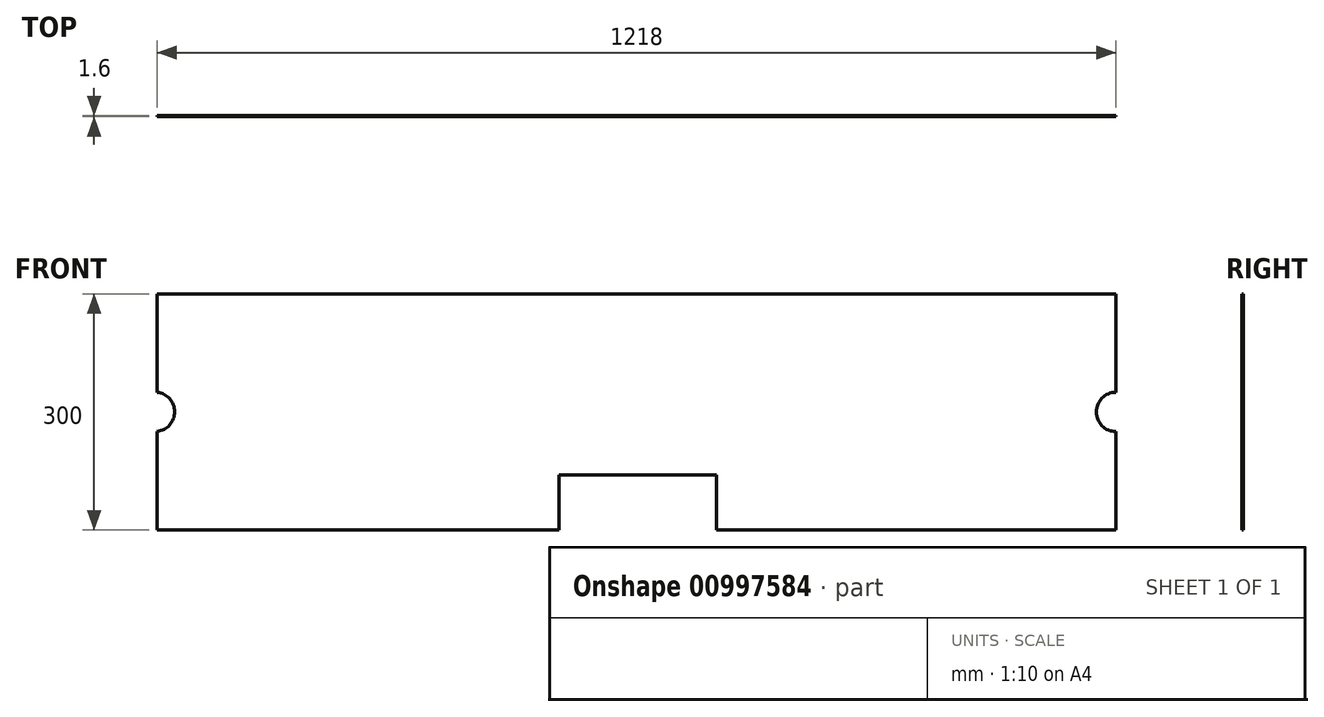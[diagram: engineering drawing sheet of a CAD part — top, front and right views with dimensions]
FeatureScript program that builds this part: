
annotation { "Feature Type Name" : "Feature", "Feature Type Description" : "" }
export const myFeature = defineFeature(function(context is Context, id is Id, definition is map)
    precondition{}
    {
        {
            var Q0;
            Q0=qCreatedBy(makeId("Front.planeOp"),FACE);
            var sketch = newSketch(context, id + "F0", { "sketchPlane" : qUnion([Q0])});
            skLineSegment(sketch, "E0.top", {"start": v(609, 150) * mm, "end": v(-609, 150) * mm});
            skLineSegment(sketch, "E0.left", {"start": v(609, -150) * mm, "end": v(609, 150) * mm});
            skLineSegment(sketch, "E0.right", {"start": v(-609, -150) * mm, "end": v(-609, 150) * mm});
            skPoint(sketch, "E0.middle", {"position": v(0, 0) * mm});
            skLineSegment(sketch, "E1", {"start": v(-609, -150) * mm, "end": v(-98.22, -150) * mm});
            skLineSegment(sketch, "E2", {"start": v(101.78, -150) * mm, "end": v(609, -150) * mm});
            skLineSegment(sketch, "E3", {"start": v(-98.22, -150) * mm, "end": v(-98.22, -80) * mm});
            skLineSegment(sketch, "E4", {"start": v(-98.22, -80) * mm, "end": v(101.78, -80) * mm});
            skLineSegment(sketch, "E5", {"start": v(101.78, -80) * mm, "end": v(101.78, -150) * mm});
            skSolve(sketch);
        }
        {
            var Q0;
            Q0 = qSketchRegion(id + "F0", true);
            extrude(context, id + "F1", {"entities" : qUnion([Q0]), "depth" : 1.6 * mm, "offsetDistance" : 25 * mm, "symmetric" : true});
        }
        {
            var Q0;
            Q0=makeQuery(id+"F1.opExtrude","CAP_FACE",FACE,{"disambiguationData":[OSD([sQuery(id+"F0.wireOp",EDGE,"E0.top"),sQuery(id+"F0.wireOp",EDGE,"E0.left"),sQuery(id+"F0.wireOp",EDGE,"E0.right"),sQuery(id+"F0.wireOp",EDGE,"E1"),sQuery(id+"F0.wireOp",EDGE,"E2"),sQuery(id+"F0.wireOp",EDGE,"E3"),sQuery(id+"F0.wireOp",EDGE,"E4"),sQuery(id+"F0.wireOp",EDGE,"E5")])],"isStart":false});
            var sketch = newSketch(context, id + "F2", { "sketchPlane" : qUnion([Q0])});
            skLineSegment(sketch, "E6", {"start": v(0, 0) * mm, "end": v(-609, 0) * mm});
            skLineSegment(sketch, "E7", {"start": v(0, 0) * mm, "end": v(609, 0) * mm});
            skLineSegment(sketch, "E8", {"start": v(-609, 0) * mm, "end": v(-435, 0) * mm});
            skLineSegment(sketch, "E9", {"start": v(-435, 0) * mm, "end": v(-261, 0) * mm});
            skLineSegment(sketch, "E10", {"start": v(-261, 0) * mm, "end": v(-87, 0) * mm});
            skLineSegment(sketch, "E11", {"start": v(-87, 0) * mm, "end": v(87, 0) * mm});
            skLineSegment(sketch, "E12", {"start": v(87, 0) * mm, "end": v(261, 0) * mm});
            skLineSegment(sketch, "E13", {"start": v(261, 0) * mm, "end": v(435, 0) * mm});
            skLineSegment(sketch, "E14", {"start": v(435, 0) * mm, "end": v(609, 0) * mm});
            skCircle(sketch, "E15", {"center": v(-435, 0) * mm, "radius": 25 * mm});
            skCircle(sketch, "E16", {"center": v(-261, 0) * mm, "radius": 25 * mm});
            skCircle(sketch, "E17", {"center": v(-87, 0) * mm, "radius": 25 * mm});
            skCircle(sketch, "E18", {"center": v(87, 0) * mm, "radius": 25 * mm});
            skCircle(sketch, "E19", {"center": v(261, 0) * mm, "radius": 25 * mm});
            skCircle(sketch, "E20", {"center": v(435, 0) * mm, "radius": 25 * mm});
            skLineSegment(sketch, "E21", {"start": v(-609, 0) * mm, "end": v(-609, 25) * mm});
            skLineSegment(sketch, "E22", {"start": v(609, 0) * mm, "end": v(609, 0) * mm});
            skLineSegment(sketch, "E23", {"start": v(609, 0) * mm, "end": v(609, 25) * mm});
            skLineSegment(sketch, "E24", {"start": v(609, 0) * mm, "end": v(609, -25) * mm});
            skLineSegment(sketch, "E25", {"start": v(-609, 0) * mm, "end": v(-609, -24.7) * mm});
            skArc(sketch, "E26", {"start": v(-609, -24.7) * mm, "mid": v(-586.71, 0.15) * mm, "end": v(-609, 25) * mm});
            skArc(sketch, "E27", {"start": v(609, 25) * mm, "mid": v(584, 0) * mm, "end": v(609, -25) * mm});
            skCircle(sketch, "E28", {"center": v(-522, 0) * mm, "radius": 10 * mm});
            skCircle(sketch, "E29", {"center": v(-348, 0) * mm, "radius": 10 * mm});
            skCircle(sketch, "E30", {"center": v(-174, 0) * mm, "radius": 10 * mm});
            skCircle(sketch, "E31", {"center": v(0, 0) * mm, "radius": 10 * mm});
            skCircle(sketch, "E32", {"center": v(174, 0) * mm, "radius": 10 * mm});
            skCircle(sketch, "E33", {"center": v(348, 0) * mm, "radius": 10 * mm});
            skCircle(sketch, "E34", {"center": v(522, 0) * mm, "radius": 10 * mm});
            skSolve(sketch);
        }
        {
            var Q0;
            {var subQ0=sQuery(id+"F2.wireOp",EDGE,"E21");Q0=makeQuery(id+"F2.imprint","IMPRINT",FACE,{"disambiguationData":[TD([[makeQuery(id+"F2.imprint","IMPRINT",EDGE,{"derivedFrom":subQ0}),-1.0]])]});}
            var Q1;
            {var subQ0=sQuery(id+"F2.wireOp",EDGE,"a51MetO8-heOr-o6G2-Rjjk-PA0d4MG9AU0j");Q1=makeQuery(id+"F2.imprint","IMPRINT",FACE,{"disambiguationData":[TD([[makeQuery(id+"F2.imprint","IMPRINT",EDGE,{"derivedFrom":subQ0}),-1.0]])]});}
            var Q2;
            {var subQ0=sQuery(id+"F2.wireOp",EDGE,"E9");var subQ1=sQuery(id+"F2.wireOp",EDGE,"E8");var subQ2=makeQuery(id+"F2.imprint","INTERSECT",VERTEX,{"derivedFrom":[subQ1,subQ0]});Q2=makeQuery(id+"F2.imprint","IMPRINT",FACE,{"disambiguationData":[TD([[makeQuery(id+"F2.imprint","IMPRINT",EDGE,{"disambiguationData":[TD([[subQ2,1.0]])],"derivedFrom":subQ1}),1.0]])]});}
            var Q3;
            {var subQ0=sQuery(id+"F2.wireOp",EDGE,"E9");var subQ1=sQuery(id+"F2.wireOp",EDGE,"E8");var subQ2=makeQuery(id+"F2.imprint","INTERSECT",VERTEX,{"derivedFrom":[subQ1,subQ0]});Q3=makeQuery(id+"F2.imprint","IMPRINT",FACE,{"disambiguationData":[TD([[makeQuery(id+"F2.imprint","IMPRINT",EDGE,{"disambiguationData":[TD([[subQ2,1.0]])],"derivedFrom":subQ1}),-1.0]])]});}
            var Q4;
            {var subQ0=sQuery(id+"F2.wireOp",EDGE,"E10");var subQ1=sQuery(id+"F2.wireOp",EDGE,"E9");var subQ2=makeQuery(id+"F2.imprint","INTERSECT",VERTEX,{"derivedFrom":[subQ1,subQ0]});Q4=makeQuery(id+"F2.imprint","IMPRINT",FACE,{"disambiguationData":[TD([[makeQuery(id+"F2.imprint","IMPRINT",EDGE,{"disambiguationData":[TD([[subQ2,1.0]])],"derivedFrom":subQ1}),1.0]])]});}
            var Q5;
            {var subQ0=sQuery(id+"F2.wireOp",EDGE,"E10");var subQ1=sQuery(id+"F2.wireOp",EDGE,"E9");var subQ2=makeQuery(id+"F2.imprint","INTERSECT",VERTEX,{"derivedFrom":[subQ1,subQ0]});Q5=makeQuery(id+"F2.imprint","IMPRINT",FACE,{"disambiguationData":[TD([[makeQuery(id+"F2.imprint","IMPRINT",EDGE,{"disambiguationData":[TD([[subQ2,1.0]])],"derivedFrom":subQ1}),-1.0]])]});}
            var Q6;
            {var subQ0=sQuery(id+"F2.wireOp",EDGE,"E11");var subQ1=sQuery(id+"F2.wireOp",EDGE,"E10");var subQ2=makeQuery(id+"F2.imprint","INTERSECT",VERTEX,{"derivedFrom":[subQ1,subQ0]});Q6=makeQuery(id+"F2.imprint","IMPRINT",FACE,{"disambiguationData":[TD([[makeQuery(id+"F2.imprint","IMPRINT",EDGE,{"disambiguationData":[TD([[subQ2,1.0]])],"derivedFrom":subQ1}),1.0]])]});}
            var Q7;
            {var subQ0=sQuery(id+"F2.wireOp",EDGE,"E11");var subQ1=sQuery(id+"F2.wireOp",EDGE,"E10");var subQ2=makeQuery(id+"F2.imprint","INTERSECT",VERTEX,{"derivedFrom":[subQ1,subQ0]});Q7=makeQuery(id+"F2.imprint","IMPRINT",FACE,{"disambiguationData":[TD([[makeQuery(id+"F2.imprint","IMPRINT",EDGE,{"disambiguationData":[TD([[subQ2,1.0]])],"derivedFrom":subQ1}),-1.0]])]});}
            var Q8;
            {var subQ0=sQuery(id+"F2.wireOp",EDGE,"E12");var subQ1=sQuery(id+"F2.wireOp",EDGE,"E11");var subQ2=makeQuery(id+"F2.imprint","INTERSECT",VERTEX,{"derivedFrom":[subQ1,subQ0]});Q8=makeQuery(id+"F2.imprint","IMPRINT",FACE,{"disambiguationData":[TD([[makeQuery(id+"F2.imprint","IMPRINT",EDGE,{"disambiguationData":[TD([[subQ2,1.0]])],"derivedFrom":subQ1}),1.0]])]});}
            var Q9;
            {var subQ0=sQuery(id+"F2.wireOp",EDGE,"E12");var subQ1=sQuery(id+"F2.wireOp",EDGE,"E11");var subQ2=makeQuery(id+"F2.imprint","INTERSECT",VERTEX,{"derivedFrom":[subQ1,subQ0]});Q9=makeQuery(id+"F2.imprint","IMPRINT",FACE,{"disambiguationData":[TD([[makeQuery(id+"F2.imprint","IMPRINT",EDGE,{"disambiguationData":[TD([[subQ2,1.0]])],"derivedFrom":subQ1}),-1.0]])]});}
            var Q10;
            {var subQ0=sQuery(id+"F2.wireOp",EDGE,"E13");var subQ1=sQuery(id+"F2.wireOp",EDGE,"E12");var subQ2=makeQuery(id+"F2.imprint","INTERSECT",VERTEX,{"derivedFrom":[subQ1,subQ0]});Q10=makeQuery(id+"F2.imprint","IMPRINT",FACE,{"disambiguationData":[TD([[makeQuery(id+"F2.imprint","IMPRINT",EDGE,{"disambiguationData":[TD([[subQ2,1.0]])],"derivedFrom":subQ1}),1.0]])]});}
            var Q11;
            {var subQ0=sQuery(id+"F2.wireOp",EDGE,"E13");var subQ1=sQuery(id+"F2.wireOp",EDGE,"E12");var subQ2=makeQuery(id+"F2.imprint","INTERSECT",VERTEX,{"derivedFrom":[subQ1,subQ0]});Q11=makeQuery(id+"F2.imprint","IMPRINT",FACE,{"disambiguationData":[TD([[makeQuery(id+"F2.imprint","IMPRINT",EDGE,{"disambiguationData":[TD([[subQ2,1.0]])],"derivedFrom":subQ1}),-1.0]])]});}
            var Q12;
            {var subQ0=sQuery(id+"F2.wireOp",EDGE,"E14");var subQ1=sQuery(id+"F2.wireOp",EDGE,"E13");var subQ2=makeQuery(id+"F2.imprint","INTERSECT",VERTEX,{"derivedFrom":[subQ1,subQ0]});Q12=makeQuery(id+"F2.imprint","IMPRINT",FACE,{"disambiguationData":[TD([[makeQuery(id+"F2.imprint","IMPRINT",EDGE,{"disambiguationData":[TD([[subQ2,1.0]])],"derivedFrom":subQ1}),1.0]])]});}
            var Q13;
            {var subQ0=sQuery(id+"F2.wireOp",EDGE,"E14");var subQ1=sQuery(id+"F2.wireOp",EDGE,"E13");var subQ2=makeQuery(id+"F2.imprint","INTERSECT",VERTEX,{"derivedFrom":[subQ1,subQ0]});Q13=makeQuery(id+"F2.imprint","IMPRINT",FACE,{"disambiguationData":[TD([[makeQuery(id+"F2.imprint","IMPRINT",EDGE,{"disambiguationData":[TD([[subQ2,1.0]])],"derivedFrom":subQ1}),-1.0]])]});}
            var Q14;
            {var subQ0=sQuery(id+"F2.wireOp",EDGE,"E22");Q14=makeQuery(id+"F2.imprint","IMPRINT",FACE,{"disambiguationData":[TD([[makeQuery(id+"F2.imprint","IMPRINT",EDGE,{"derivedFrom":subQ0}),1.0]])]});}
            var Q15;
            {var subQ0=sQuery(id+"F2.wireOp",EDGE,"DOqnfdGX-DpiK-KGu9-LrKi-PVQsx8hhRL7E");Q15=makeQuery(id+"F2.imprint","IMPRINT",FACE,{"disambiguationData":[TD([[makeQuery(id+"F2.imprint","IMPRINT",EDGE,{"derivedFrom":subQ0}),1.0]])]});}
            var Q16;
            {var subQ0=sQuery(id+"F2.wireOp",EDGE,"E25");Q16=makeQuery(id+"F2.imprint","IMPRINT",FACE,{"disambiguationData":[TD([[makeQuery(id+"F2.imprint","IMPRINT",EDGE,{"derivedFrom":subQ0}),-1.0]])]});}
            var Q17;
            {var subQ0=sQuery(id+"F2.wireOp",EDGE,"E23");Q17=makeQuery(id+"F2.imprint","IMPRINT",FACE,{"disambiguationData":[TD([[makeQuery(id+"F2.imprint","IMPRINT",EDGE,{"derivedFrom":subQ0}),1.0]])]});}
            var Q18;
            {var subQ0=sQuery(id+"F2.wireOp",EDGE,"E24");Q18=makeQuery(id+"F2.imprint","IMPRINT",FACE,{"disambiguationData":[TD([[makeQuery(id+"F2.imprint","IMPRINT",EDGE,{"derivedFrom":subQ0}),1.0]])]});}
            var Q19;
            {var subQ0=sQuery(id+"F2.wireOp",EDGE,"E28");var subQ1=sQuery(id+"F2.wireOp",EDGE,"E8");var subQ2=makeQuery(id+"F2.imprint","INTERSECT",VERTEX,{"disambiguationData":[OD(0.0)],"derivedFrom":[subQ1,subQ0]});Q19=makeQuery(id+"F2.imprint","IMPRINT",FACE,{"disambiguationData":[TD([[makeQuery(id+"F2.imprint","IMPRINT",EDGE,{"disambiguationData":[TD([[subQ2,-1.0]])],"derivedFrom":subQ1}),1.0]])]});}
            var Q20;
            {var subQ0=sQuery(id+"F2.wireOp",EDGE,"E28");var subQ1=sQuery(id+"F2.wireOp",EDGE,"E8");var subQ2=makeQuery(id+"F2.imprint","INTERSECT",VERTEX,{"disambiguationData":[OD(0.0)],"derivedFrom":[subQ1,subQ0]});Q20=makeQuery(id+"F2.imprint","IMPRINT",FACE,{"disambiguationData":[TD([[makeQuery(id+"F2.imprint","IMPRINT",EDGE,{"disambiguationData":[TD([[subQ2,-1.0]])],"derivedFrom":subQ1}),-1.0]])]});}
            var Q21;
            {var subQ0=sQuery(id+"F2.wireOp",EDGE,"E29");var subQ1=sQuery(id+"F2.wireOp",EDGE,"E9");var subQ2=makeQuery(id+"F2.imprint","INTERSECT",VERTEX,{"disambiguationData":[OD(0.0)],"derivedFrom":[subQ1,subQ0]});Q21=makeQuery(id+"F2.imprint","IMPRINT",FACE,{"disambiguationData":[TD([[makeQuery(id+"F2.imprint","IMPRINT",EDGE,{"disambiguationData":[TD([[subQ2,-1.0]])],"derivedFrom":subQ1}),1.0]])]});}
            var Q22;
            {var subQ0=sQuery(id+"F2.wireOp",EDGE,"E29");var subQ1=sQuery(id+"F2.wireOp",EDGE,"E9");var subQ2=makeQuery(id+"F2.imprint","INTERSECT",VERTEX,{"disambiguationData":[OD(0.0)],"derivedFrom":[subQ1,subQ0]});Q22=makeQuery(id+"F2.imprint","IMPRINT",FACE,{"disambiguationData":[TD([[makeQuery(id+"F2.imprint","IMPRINT",EDGE,{"disambiguationData":[TD([[subQ2,-1.0]])],"derivedFrom":subQ1}),-1.0]])]});}
            var Q23;
            {var subQ0=sQuery(id+"F2.wireOp",EDGE,"E30");var subQ1=sQuery(id+"F2.wireOp",EDGE,"E10");var subQ2=makeQuery(id+"F2.imprint","INTERSECT",VERTEX,{"disambiguationData":[OD(0.0)],"derivedFrom":[subQ1,subQ0]});Q23=makeQuery(id+"F2.imprint","IMPRINT",FACE,{"disambiguationData":[TD([[makeQuery(id+"F2.imprint","IMPRINT",EDGE,{"disambiguationData":[TD([[subQ2,-1.0]])],"derivedFrom":subQ1}),1.0]])]});}
            var Q24;
            {var subQ0=sQuery(id+"F2.wireOp",EDGE,"E30");var subQ1=sQuery(id+"F2.wireOp",EDGE,"E10");var subQ2=makeQuery(id+"F2.imprint","INTERSECT",VERTEX,{"disambiguationData":[OD(0.0)],"derivedFrom":[subQ1,subQ0]});Q24=makeQuery(id+"F2.imprint","IMPRINT",FACE,{"disambiguationData":[TD([[makeQuery(id+"F2.imprint","IMPRINT",EDGE,{"disambiguationData":[TD([[subQ2,-1.0]])],"derivedFrom":subQ1}),-1.0]])]});}
            var Q25;
            {var subQ0=sQuery(id+"F2.wireOp",EDGE,"E31");var subQ1=sQuery(id+"F2.wireOp",EDGE,"E11");var subQ2=makeQuery(id+"F2.imprint","INTERSECT",VERTEX,{"disambiguationData":[OD(0.0)],"derivedFrom":[subQ1,subQ0]});Q25=makeQuery(id+"F2.imprint","IMPRINT",FACE,{"disambiguationData":[TD([[makeQuery(id+"F2.imprint","IMPRINT",EDGE,{"disambiguationData":[TD([[subQ2,-1.0]])],"derivedFrom":subQ1}),1.0]])]});}
            var Q26;
            {var subQ0=sQuery(id+"F2.wireOp",EDGE,"E31");var subQ1=sQuery(id+"F2.wireOp",EDGE,"E11");var subQ2=makeQuery(id+"F2.imprint","INTERSECT",VERTEX,{"disambiguationData":[OD(0.0)],"derivedFrom":[subQ1,subQ0]});Q26=makeQuery(id+"F2.imprint","IMPRINT",FACE,{"disambiguationData":[TD([[makeQuery(id+"F2.imprint","IMPRINT",EDGE,{"disambiguationData":[TD([[subQ2,-1.0]])],"derivedFrom":subQ1}),-1.0]])]});}
            var Q27;
            {var subQ0=sQuery(id+"F2.wireOp",EDGE,"E32");var subQ1=sQuery(id+"F2.wireOp",EDGE,"E12");var subQ2=makeQuery(id+"F2.imprint","INTERSECT",VERTEX,{"disambiguationData":[OD(0.0)],"derivedFrom":[subQ1,subQ0]});Q27=makeQuery(id+"F2.imprint","IMPRINT",FACE,{"disambiguationData":[TD([[makeQuery(id+"F2.imprint","IMPRINT",EDGE,{"disambiguationData":[TD([[subQ2,-1.0]])],"derivedFrom":subQ1}),1.0]])]});}
            var Q28;
            {var subQ0=sQuery(id+"F2.wireOp",EDGE,"E32");var subQ1=sQuery(id+"F2.wireOp",EDGE,"E12");var subQ2=makeQuery(id+"F2.imprint","INTERSECT",VERTEX,{"disambiguationData":[OD(0.0)],"derivedFrom":[subQ1,subQ0]});Q28=makeQuery(id+"F2.imprint","IMPRINT",FACE,{"disambiguationData":[TD([[makeQuery(id+"F2.imprint","IMPRINT",EDGE,{"disambiguationData":[TD([[subQ2,-1.0]])],"derivedFrom":subQ1}),-1.0]])]});}
            var Q29;
            {var subQ0=sQuery(id+"F2.wireOp",EDGE,"E33");var subQ1=sQuery(id+"F2.wireOp",EDGE,"E13");var subQ2=makeQuery(id+"F2.imprint","INTERSECT",VERTEX,{"disambiguationData":[OD(0.0)],"derivedFrom":[subQ1,subQ0]});Q29=makeQuery(id+"F2.imprint","IMPRINT",FACE,{"disambiguationData":[TD([[makeQuery(id+"F2.imprint","IMPRINT",EDGE,{"disambiguationData":[TD([[subQ2,-1.0]])],"derivedFrom":subQ1}),1.0]])]});}
            var Q30;
            {var subQ0=sQuery(id+"F2.wireOp",EDGE,"E33");var subQ1=sQuery(id+"F2.wireOp",EDGE,"E13");var subQ2=makeQuery(id+"F2.imprint","INTERSECT",VERTEX,{"disambiguationData":[OD(0.0)],"derivedFrom":[subQ1,subQ0]});Q30=makeQuery(id+"F2.imprint","IMPRINT",FACE,{"disambiguationData":[TD([[makeQuery(id+"F2.imprint","IMPRINT",EDGE,{"disambiguationData":[TD([[subQ2,-1.0]])],"derivedFrom":subQ1}),-1.0]])]});}
            var Q31;
            {var subQ0=sQuery(id+"F2.wireOp",EDGE,"E34");var subQ1=sQuery(id+"F2.wireOp",EDGE,"E14");var subQ2=makeQuery(id+"F2.imprint","INTERSECT",VERTEX,{"disambiguationData":[OD(0.0)],"derivedFrom":[subQ1,subQ0]});Q31=makeQuery(id+"F2.imprint","IMPRINT",FACE,{"disambiguationData":[TD([[makeQuery(id+"F2.imprint","IMPRINT",EDGE,{"disambiguationData":[TD([[subQ2,-1.0]])],"derivedFrom":subQ1}),1.0]])]});}
            var Q32;
            {var subQ0=sQuery(id+"F2.wireOp",EDGE,"E34");var subQ1=sQuery(id+"F2.wireOp",EDGE,"E14");var subQ2=makeQuery(id+"F2.imprint","INTERSECT",VERTEX,{"disambiguationData":[OD(0.0)],"derivedFrom":[subQ1,subQ0]});Q32=makeQuery(id+"F2.imprint","IMPRINT",FACE,{"disambiguationData":[TD([[makeQuery(id+"F2.imprint","IMPRINT",EDGE,{"disambiguationData":[TD([[subQ2,-1.0]])],"derivedFrom":subQ1}),-1.0]])]});}
            extrude(context, id + "F3", {"entities" : qUnion([Q0, Q1, Q2, Q3, Q4, Q5, Q6, Q7, Q8, Q9, Q10, Q11, Q12, Q13, Q14, Q15, Q16, Q17, Q18, Q19, Q20, Q21, Q22, Q23, Q24, Q25, Q26, Q27, Q28, Q29, Q30, Q31, Q32]), "operationType" : NewBodyOperationType.REMOVE, "oppositeDirection" : true, "depth" : 25 * mm, "offsetDistance" : 25 * mm});
        }
    });
